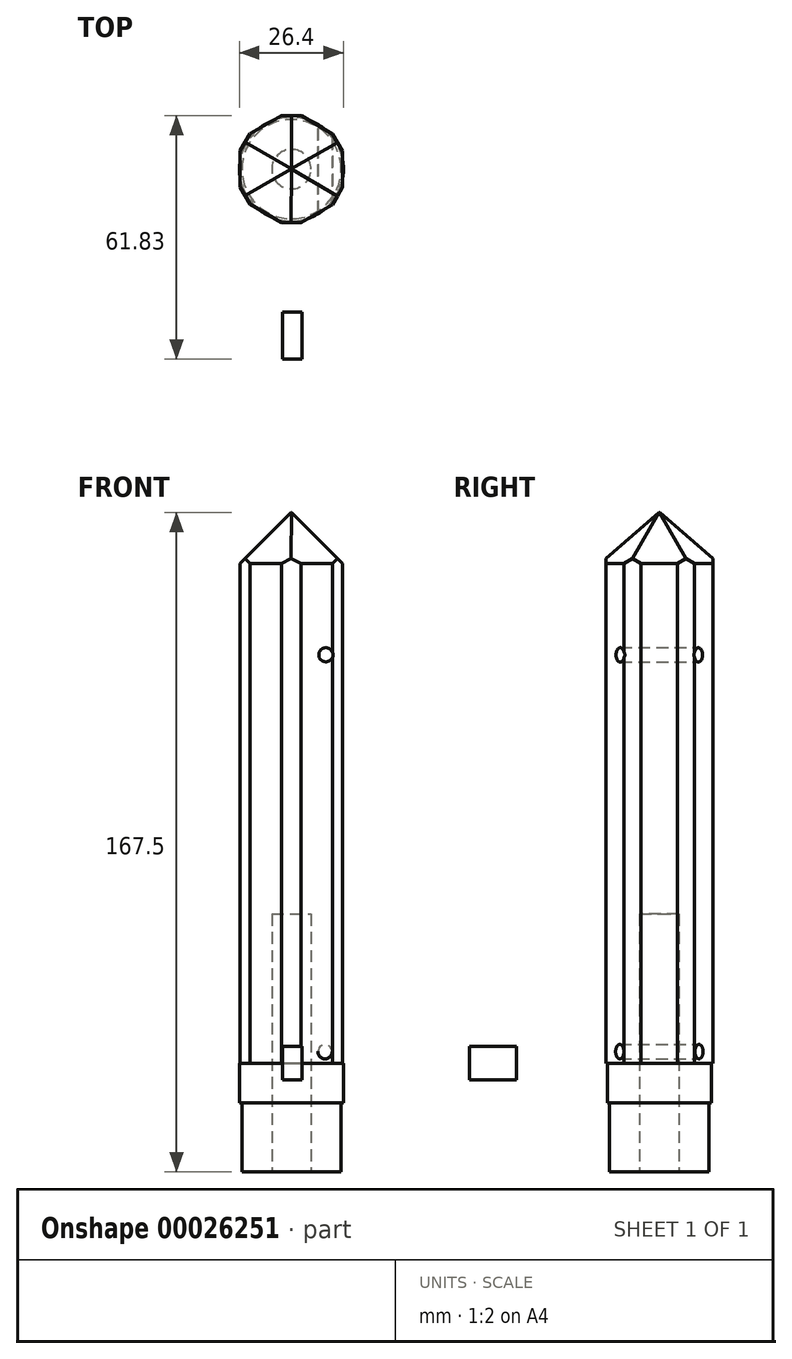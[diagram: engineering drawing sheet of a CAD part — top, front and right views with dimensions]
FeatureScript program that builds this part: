
annotation { "Feature Type Name" : "Feature", "Feature Type Description" : "" }
export const myFeature = defineFeature(function(context is Context, id is Id, definition is map)
    precondition{}
    {
        {
            var Q0;
            Q0=qCreatedBy(makeId("Front.planeOp"),FACE);
            var sketch = newSketch(context, id + "F0", { "sketchPlane" : qUnion([Q0])});
            skLineSegment(sketch, "E0.bottom", {"start": v(-84.2, -32.3) * mm, "end": v(45.8, -32.3) * mm});
            skLineSegment(sketch, "E0.top", {"start": v(-84.2, 37.7) * mm, "end": v(45.8, 37.7) * mm});
            skLineSegment(sketch, "E0.left", {"start": v(-84.2, -32.3) * mm, "end": v(-84.2, 37.7) * mm});
            skLineSegment(sketch, "E0.right", {"start": v(45.8, -32.3) * mm, "end": v(45.8, 37.7) * mm});
            skSolve(sketch);
        }
        {
            var Q0;
            Q0=makeQuery(id+"F0.imprint","IMPRINT",FACE,{"disambiguationData":[TD([[makeQuery(id+"F0.imprint","IMPRINT",EDGE,{"derivedFrom":sQuery(id+"F0.wireOp",EDGE,"E0.bottom")}),1.0]])]});
            extrude(context, id + "F1", {"entities" : qUnion([Q0]), "depth" : 40 * mm});
        }
        {
            var Q0;
            Q0=makeQuery(id+"F1.opExtrude","SWEPT_FACE",FACE,{"disambiguationData":[OSD([sQuery(id+"F0.wireOp",EDGE,"E0.left")])]});
            var sketch = newSketch(context, id + "F2", { "sketchPlane" : qUnion([Q0])});
            skCircle(sketch, "E1", {"center": v(20, 2.7) * mm, "radius": 5 * mm});
            skCircle(sketch, "E2", {"center": v(20, 2.7) * mm, "radius": 15 * mm});
            skCircle(sketch, "E3.cCircle", {"center": v(20, 2.7) * mm, "radius": 15 * mm, "construction": true});
            skLineSegment(sketch, "E3.0", {"start": v(27.46, 15.71) * mm, "end": v(35, 2.74) * mm});
            skLineSegment(sketch, "E3.1", {"start": v(35, 2.74) * mm, "end": v(27.54, -10.27) * mm});
            skLineSegment(sketch, "E3.2", {"start": v(27.54, -10.27) * mm, "end": v(12.54, -10.3) * mm});
            skLineSegment(sketch, "E3.3", {"start": v(12.54, -10.3) * mm, "end": v(5, 2.66) * mm});
            skLineSegment(sketch, "E3.4", {"start": v(5, 2.66) * mm, "end": v(12.46, 15.67) * mm});
            skLineSegment(sketch, "E3.5", {"start": v(12.46, 15.67) * mm, "end": v(27.46, 15.71) * mm});
            skSolve(sketch);
        }
        {
            var Q0;
            Q0=makeQuery(id+"F1.opExtrude","CAP_FACE",FACE,{"disambiguationData":[OSD([sQuery(id+"F0.wireOp",EDGE,"E0.bottom"),sQuery(id+"F0.wireOp",EDGE,"E0.top"),sQuery(id+"F0.wireOp",EDGE,"E0.left"),sQuery(id+"F0.wireOp",EDGE,"E0.right")])],"isStart":false});
            var sketch = newSketch(context, id + "F3", { "sketchPlane" : qUnion([Q0])});
            skCircle(sketch, "E4", {"center": v(-35.56, -24.64) * mm, "radius": 2 * mm});
            skCircle(sketch, "E5", {"center": v(174.33, -24.64) * mm, "radius": 2 * mm});
            skSolve(sketch);
        }
        {
            var Q0;
            Q0=makeQuery(id+"F3.imprint","IMPRINT",FACE,{"disambiguationData":[TD([[makeQuery(id+"F3.imprint","IMPRINT",EDGE,{"derivedFrom":sQuery(id+"F3.wireOp",EDGE,"E4")}),1.0]])]});
            var Q1;
            Q1=makeQuery(id+"F3.imprint","IMPRINT",FACE,{"disambiguationData":[TD([[makeQuery(id+"F3.imprint","IMPRINT",EDGE,{"derivedFrom":sQuery(id+"F3.wireOp",EDGE,"E5")}),1.0]])]});
            extrude(context, id + "F4", {"entities" : qUnion([Q0, Q1]), "operationType" : NewBodyOperationType.REMOVE, "endBound" : BoundingType.THROUGH_ALL, "oppositeDirection" : true, "depth" : 25 * mm});
        }
        {
            var Q0;
            {var subQ0=sQuery(id+"F0.wireOp",EDGE,"E0.left");Q0=makeQuery(id+"F2.imprint","IMPRINT",FACE,{"disambiguationData":[TD([[makeQuery(id+"F2.imprint","IMPRINT",EDGE,{"derivedFrom":makeQuery(id+"F1.opExtrude","CAP_EDGE",EDGE,{"disambiguationData":[OSD([subQ0])],"isStart":true})}),-1.0]])]});}
            extrude(context, id + "F5", {"entities" : qUnion([Q0]), "operationType" : NewBodyOperationType.REMOVE, "endBound" : BoundingType.THROUGH_ALL, "oppositeDirection" : true, "depth" : 25 * mm});
        }
        {
            var Q0;
            {var subQ0=sQuery(id+"F2.wireOp",EDGE,"E3.4");Q0=makeQuery(id+"F2.imprint","IMPRINT",FACE,{"disambiguationData":[TD([[makeQuery(id+"F2.imprint","IMPRINT",EDGE,{"derivedFrom":subQ0}),1.0]])]});}
            var Q1;
            {var subQ0=sQuery(id+"F2.wireOp",EDGE,"E3.5");Q1=makeQuery(id+"F2.imprint","IMPRINT",FACE,{"disambiguationData":[TD([[makeQuery(id+"F2.imprint","IMPRINT",EDGE,{"derivedFrom":subQ0}),1.0]])]});}
            var Q2;
            {var subQ0=sQuery(id+"F2.wireOp",EDGE,"E3.0");Q2=makeQuery(id+"F2.imprint","IMPRINT",FACE,{"disambiguationData":[TD([[makeQuery(id+"F2.imprint","IMPRINT",EDGE,{"derivedFrom":subQ0}),1.0]])]});}
            var Q3;
            {var subQ0=sQuery(id+"F2.wireOp",EDGE,"E3.1");Q3=makeQuery(id+"F2.imprint","IMPRINT",FACE,{"disambiguationData":[TD([[makeQuery(id+"F2.imprint","IMPRINT",EDGE,{"derivedFrom":subQ0}),1.0]])]});}
            var Q4;
            {var subQ0=sQuery(id+"F2.wireOp",EDGE,"E3.2");Q4=makeQuery(id+"F2.imprint","IMPRINT",FACE,{"disambiguationData":[TD([[makeQuery(id+"F2.imprint","IMPRINT",EDGE,{"derivedFrom":subQ0}),1.0]])]});}
            var Q5;
            {var subQ0=sQuery(id+"F2.wireOp",EDGE,"E3.3");Q5=makeQuery(id+"F2.imprint","IMPRINT",FACE,{"disambiguationData":[TD([[makeQuery(id+"F2.imprint","IMPRINT",EDGE,{"derivedFrom":subQ0}),1.0]])]});}
            extrude(context, id + "F6", {"entities" : qUnion([Q0, Q1, Q2, Q3, Q4, Q5]), "operationType" : NewBodyOperationType.REMOVE, "endBound" : BoundingType.THROUGH_ALL, "oppositeDirection" : true, "depth" : 25 * mm});
        }
        {
            var Q0;
            Q0=makeQuery(id+"F1.opExtrude","SWEPT_FACE",FACE,{"disambiguationData":[OSD([sQuery(id+"F0.wireOp",EDGE,"E0.right")])]});
            extrude(context, id + "F7", {"entities" : qUnion([Q0]), "operationType" : NewBodyOperationType.ADD, "depth" : 30 * mm});
        }
        {
            var Q0;
            Q0=makeQuery(id+"F7.opExtrude","CAP_EDGE",EDGE,{"disambiguationData":[OSD([sQuery(id+"F0.wireOp",EDGE,"E0.right"),sQuery(id+"F2.wireOp",EDGE,"E3.5")])],"isStart":false});
            var Q1;
            Q1=makeQuery(id+"F7.opExtrude","CAP_EDGE",EDGE,{"disambiguationData":[OSD([sQuery(id+"F0.wireOp",EDGE,"E0.right"),sQuery(id+"F2.wireOp",EDGE,"E3.0")])],"isStart":false});
            var Q2;
            Q2=makeQuery(id+"F7.opExtrude","CAP_EDGE",EDGE,{"disambiguationData":[OSD([sQuery(id+"F0.wireOp",EDGE,"E0.right"),sQuery(id+"F2.wireOp",EDGE,"E3.4")])],"isStart":false});
            var Q3;
            Q3=makeQuery(id+"F7.opExtrude","CAP_EDGE",EDGE,{"disambiguationData":[OSD([sQuery(id+"F0.wireOp",EDGE,"E0.right"),sQuery(id+"F2.wireOp",EDGE,"E3.3")])],"isStart":false});
            var Q4;
            Q4=makeQuery(id+"F7.opExtrude","CAP_EDGE",EDGE,{"disambiguationData":[OSD([sQuery(id+"F0.wireOp",EDGE,"E0.right"),sQuery(id+"F2.wireOp",EDGE,"E3.1")])],"isStart":false});
            var Q5;
            Q5=makeQuery(id+"F7.opExtrude","CAP_EDGE",EDGE,{"disambiguationData":[OSD([sQuery(id+"F0.wireOp",EDGE,"E0.right"),sQuery(id+"F2.wireOp",EDGE,"E3.2")])],"isStart":false});
            chamfer(context, id + "F8", {"entities" : qUnion([Q0, Q1, Q2, Q3, Q4, Q5]), "width" : 12.9 * mm, "tangentPropagation" : true});
        }
        {
            var Q0;
            {var subQ0=sQuery(id+"F2.wireOp",EDGE,"E2");var subQ1=sQuery(id+"F2.wireOp",EDGE,"E3.0");var subQ2=sQuery(id+"F2.wireOp",EDGE,"E3.5");Q0=makeQuery(id+"F7.boolean.opBoolean","MERGE",EDGE,{"derivedFrom":[makeQuery(id+"F6.boolean.opBoolean","TWEAK_EDGE",EDGE,{"derivedFrom":[makeQuery(id+"F6.opExtrude","SWEPT_EDGE",EDGE,{"disambiguationData":[OSD([subQ0,subQ1,subQ2]),ownerDisambiguation([makeQuery(id+"F6.opExtrude","SWEPT_BODY",BODY,{"disambiguationData":[OSD([subQ0,subQ1])]})])]}),makeQuery(id+"F6.opExtrude","SWEPT_EDGE",EDGE,{"disambiguationData":[OSD([subQ0,subQ1,subQ2]),ownerDisambiguation([makeQuery(id+"F6.opExtrude","SWEPT_BODY",BODY,{"disambiguationData":[OSD([subQ0,subQ2])]})])]})]}),makeQuery(id+"F7.opExtrude","SWEPT_EDGE",EDGE,{"disambiguationData":[OSD([sQuery(id+"F0.wireOp",EDGE,"E0.right"),subQ1,subQ2])]})]});}
            var Q1;
            {var subQ0=sQuery(id+"F2.wireOp",EDGE,"E2");var subQ1=sQuery(id+"F2.wireOp",EDGE,"E3.4");var subQ2=sQuery(id+"F2.wireOp",EDGE,"E3.5");Q1=makeQuery(id+"F7.boolean.opBoolean","MERGE",EDGE,{"derivedFrom":[makeQuery(id+"F6.boolean.opBoolean","TWEAK_EDGE",EDGE,{"derivedFrom":[makeQuery(id+"F6.opExtrude","SWEPT_EDGE",EDGE,{"disambiguationData":[OSD([subQ0,subQ1,subQ2]),ownerDisambiguation([makeQuery(id+"F6.opExtrude","SWEPT_BODY",BODY,{"disambiguationData":[OSD([subQ0,subQ2])]})])]}),makeQuery(id+"F6.opExtrude","SWEPT_EDGE",EDGE,{"disambiguationData":[OSD([subQ0,subQ1,subQ2]),ownerDisambiguation([makeQuery(id+"F6.opExtrude","SWEPT_BODY",BODY,{"disambiguationData":[OSD([subQ0,subQ1])]})])]})]}),makeQuery(id+"F7.opExtrude","SWEPT_EDGE",EDGE,{"disambiguationData":[OSD([sQuery(id+"F0.wireOp",EDGE,"E0.right"),subQ1,subQ2])]})]});}
            var Q2;
            {var subQ0=sQuery(id+"F2.wireOp",EDGE,"E2");var subQ1=sQuery(id+"F2.wireOp",EDGE,"E3.0");var subQ2=sQuery(id+"F2.wireOp",EDGE,"E3.1");Q2=makeQuery(id+"F7.boolean.opBoolean","MERGE",EDGE,{"derivedFrom":[makeQuery(id+"F6.boolean.opBoolean","TWEAK_EDGE",EDGE,{"derivedFrom":[makeQuery(id+"F6.opExtrude","SWEPT_EDGE",EDGE,{"disambiguationData":[OSD([subQ0,subQ1,subQ2]),ownerDisambiguation([makeQuery(id+"F6.opExtrude","SWEPT_BODY",BODY,{"disambiguationData":[OSD([subQ0,subQ1])]})])]}),makeQuery(id+"F6.opExtrude","SWEPT_EDGE",EDGE,{"disambiguationData":[OSD([subQ0,subQ1,subQ2]),ownerDisambiguation([makeQuery(id+"F6.opExtrude","SWEPT_BODY",BODY,{"disambiguationData":[OSD([subQ0,subQ2])]})])]})]}),makeQuery(id+"F7.opExtrude","SWEPT_EDGE",EDGE,{"disambiguationData":[OSD([sQuery(id+"F0.wireOp",EDGE,"E0.right"),subQ1,subQ2])]})]});}
            var Q3;
            {var subQ0=sQuery(id+"F2.wireOp",EDGE,"E2");var subQ1=sQuery(id+"F2.wireOp",EDGE,"E3.1");var subQ2=sQuery(id+"F2.wireOp",EDGE,"E3.2");Q3=makeQuery(id+"F7.boolean.opBoolean","MERGE",EDGE,{"derivedFrom":[makeQuery(id+"F6.boolean.opBoolean","TWEAK_EDGE",EDGE,{"derivedFrom":[makeQuery(id+"F6.opExtrude","SWEPT_EDGE",EDGE,{"disambiguationData":[OSD([subQ0,subQ1,subQ2]),ownerDisambiguation([makeQuery(id+"F6.opExtrude","SWEPT_BODY",BODY,{"disambiguationData":[OSD([subQ0,subQ2])]})])]}),makeQuery(id+"F6.opExtrude","SWEPT_EDGE",EDGE,{"disambiguationData":[OSD([subQ0,subQ1,subQ2]),ownerDisambiguation([makeQuery(id+"F6.opExtrude","SWEPT_BODY",BODY,{"disambiguationData":[OSD([subQ0,subQ1])]})])]})]}),makeQuery(id+"F7.opExtrude","SWEPT_EDGE",EDGE,{"disambiguationData":[OSD([sQuery(id+"F0.wireOp",EDGE,"E0.right"),subQ1,subQ2])]})]});}
            var Q4;
            {var subQ0=sQuery(id+"F2.wireOp",EDGE,"E2");var subQ1=sQuery(id+"F2.wireOp",EDGE,"E3.3");var subQ2=sQuery(id+"F2.wireOp",EDGE,"E3.4");Q4=makeQuery(id+"F7.boolean.opBoolean","MERGE",EDGE,{"derivedFrom":[makeQuery(id+"F6.boolean.opBoolean","TWEAK_EDGE",EDGE,{"derivedFrom":[makeQuery(id+"F6.opExtrude","SWEPT_EDGE",EDGE,{"disambiguationData":[OSD([subQ0,subQ1,subQ2]),ownerDisambiguation([makeQuery(id+"F6.opExtrude","SWEPT_BODY",BODY,{"disambiguationData":[OSD([subQ0,subQ2])]})])]}),makeQuery(id+"F6.opExtrude","SWEPT_EDGE",EDGE,{"disambiguationData":[OSD([subQ0,subQ1,subQ2]),ownerDisambiguation([makeQuery(id+"F6.opExtrude","SWEPT_BODY",BODY,{"disambiguationData":[OSD([subQ0,subQ1])]})])]})]}),makeQuery(id+"F7.opExtrude","SWEPT_EDGE",EDGE,{"disambiguationData":[OSD([sQuery(id+"F0.wireOp",EDGE,"E0.right"),subQ1,subQ2])]})]});}
            var Q5;
            {var subQ0=sQuery(id+"F2.wireOp",EDGE,"E2");var subQ1=sQuery(id+"F2.wireOp",EDGE,"E3.2");var subQ2=sQuery(id+"F2.wireOp",EDGE,"E3.3");Q5=makeQuery(id+"F7.boolean.opBoolean","MERGE",EDGE,{"derivedFrom":[makeQuery(id+"F6.boolean.opBoolean","TWEAK_EDGE",EDGE,{"derivedFrom":[makeQuery(id+"F6.opExtrude","SWEPT_EDGE",EDGE,{"disambiguationData":[OSD([subQ0,subQ1,subQ2]),ownerDisambiguation([makeQuery(id+"F6.opExtrude","SWEPT_BODY",BODY,{"disambiguationData":[OSD([subQ0,subQ2])]})])]}),makeQuery(id+"F6.opExtrude","SWEPT_EDGE",EDGE,{"disambiguationData":[OSD([subQ0,subQ1,subQ2]),ownerDisambiguation([makeQuery(id+"F6.opExtrude","SWEPT_BODY",BODY,{"disambiguationData":[OSD([subQ0,subQ1])]})])]})]}),makeQuery(id+"F7.opExtrude","SWEPT_EDGE",EDGE,{"disambiguationData":[OSD([sQuery(id+"F0.wireOp",EDGE,"E0.right"),subQ1,subQ2])]})]});}
            chamfer(context, id + "F9", {"entities" : qUnion([Q0, Q1, Q2, Q3, Q4, Q5]), "width" : 5 * mm, "tangentPropagation" : true});
        }
        {
            var Q0;
            Q0=qCreatedBy(makeId("Front.planeOp"),FACE);
            var sketch = newSketch(context, id + "F10", { "sketchPlane" : qUnion([Q0])});
            skCircle(sketch, "E6", {"center": v(-61.16, -5.86) * mm, "radius": 1.83 * mm});
            skCircle(sketch, "E7", {"center": v(39.65, -6.06) * mm, "radius": 1.83 * mm});
            skSolve(sketch);
        }
        {
            var Q0;
            Q0=makeQuery(id+"F10.imprint","IMPRINT",FACE,{"disambiguationData":[TD([[makeQuery(id+"F10.imprint","IMPRINT",EDGE,{"derivedFrom":sQuery(id+"F10.wireOp",EDGE,"E7")}),1.0]])]});
            var Q1;
            Q1=makeQuery(id+"F10.imprint","IMPRINT",FACE,{"disambiguationData":[TD([[makeQuery(id+"F10.imprint","IMPRINT",EDGE,{"derivedFrom":sQuery(id+"F10.wireOp",EDGE,"E6")}),1.0]])]});
            extrude(context, id + "F11", {"entities" : qUnion([Q0, Q1]), "operationType" : NewBodyOperationType.REMOVE, "endBound" : BoundingType.THROUGH_ALL, "depth" : 25 * mm});
        }
        {
            var Q0;
            Q0=makeQuery(id+"F1.opExtrude","SWEPT_FACE",FACE,{"disambiguationData":[OSD([sQuery(id+"F0.wireOp",EDGE,"E0.left")])]});
            extrude(context, id + "F12", {"entities" : qUnion([Q0]), "operationType" : NewBodyOperationType.REMOVE, "oppositeDirection" : true, "depth" : 20 * mm});
        }
        {
            var Q0;
            Q0=makeQuery(id+"F12.boolean.opBoolean","COPY",FACE,{"derivedFrom":makeQuery(id+"F12.opExtrude","CAP_FACE",FACE,{"disambiguationData":[OSD([sQuery(id+"F0.wireOp",EDGE,"E0.left")])],"isStart":false})});
            var sketch = newSketch(context, id + "F13", { "sketchPlane" : qUnion([Q0])});
            skPoint(sketch, "E8", {"position": v(20.02, 2.68) * mm});
            skCircle(sketch, "E9", {"center": v(20.02, 2.68) * mm, "radius": 13.2 * mm});
            skSolve(sketch);
        }
        {
            var Q0;
            Q0=qSketchRegion(id+"F13",true);
            extrude(context, id + "F14", {"entities" : qUnion([Q0]), "operationType" : NewBodyOperationType.ADD, "depth" : 10 * mm});
        }
        {
            var Q0;
            Q0=makeQuery(id+"F14.opExtrude","CAP_FACE",FACE,{"disambiguationData":[OSD([sQuery(id+"F13.wireOp",EDGE,"E9")])],"isStart":false});
            var sketch = newSketch(context, id + "F15", { "sketchPlane" : qUnion([Q0])});
            skCircle(sketch, "E10", {"center": v(20.02, 2.68) * mm, "radius": 12.6 * mm});
            skSolve(sketch);
        }
        {
            var Q0;
            Q0=qSketchRegion(id+"F15",true);
            extrude(context, id + "F16", {"entities" : qUnion([Q0]), "operationType" : NewBodyOperationType.ADD, "depth" : 17.5 * mm});
        }
        {
            var Q0;
            Q0=makeQuery(id+"F16.opExtrude","CAP_FACE",FACE,{"disambiguationData":[OSD([sQuery(id+"F15.wireOp",EDGE,"E10")])],"isStart":false});
            var sketch = newSketch(context, id + "F17", { "sketchPlane" : qUnion([Q0])});
            skCircle(sketch, "E11", {"center": v(20.02, 2.68) * mm, "radius": 5 * mm});
            skSolve(sketch);
        }
        {
            var Q0;
            Q0=makeQuery(id+"F17.imprint","IMPRINT",FACE,{"disambiguationData":[TD([[makeQuery(id+"F17.imprint","IMPRINT",EDGE,{"derivedFrom":sQuery(id+"F17.wireOp",EDGE,"E11")}),1.0]])]});
            extrude(context, id + "F18", {"entities" : qUnion([Q0]), "operationType" : NewBodyOperationType.REMOVE, "oppositeDirection" : true, "depth" : 65.5 * mm});
        }
        {
            var Q0;
            Q0=qCreatedBy(makeId("Top.planeOp"),FACE);
            var sketch = newSketch(context, id + "F19", { "sketchPlane" : qUnion([Q0])});
            skLineSegment(sketch, "E12.bottom", {"start": v(-68.34, -68.27) * mm, "end": v(-59.86, -68.27) * mm});
            skLineSegment(sketch, "E12.top", {"start": v(-68.34, -56.3) * mm, "end": v(-59.86, -56.3) * mm});
            skLineSegment(sketch, "E12.left", {"start": v(-68.34, -68.27) * mm, "end": v(-68.34, -56.3) * mm});
            skLineSegment(sketch, "E12.right", {"start": v(-59.86, -68.27) * mm, "end": v(-59.86, -56.3) * mm});
            skSolve(sketch);
        }
        {
            var Q0;
            Q0=makeQuery(id+"F19.imprint","IMPRINT",FACE,{"disambiguationData":[TD([[makeQuery(id+"F19.imprint","IMPRINT",EDGE,{"derivedFrom":sQuery(id+"F19.wireOp",EDGE,"E12.bottom")}),1.0]])]});
            extrude(context, id + "F20", {"entities" : qUnion([Q0]), "depth" : 5 * mm});
        }
        {
            var Q0;
            Q0=makeQuery(id+"F1.opExtrude","SWEPT_BODY",BODY,{"disambiguationData":[OSD([sQuery(id+"F0.wireOp",EDGE,"E0.bottom"),sQuery(id+"F0.wireOp",EDGE,"E0.top"),sQuery(id+"F0.wireOp",EDGE,"E0.left"),sQuery(id+"F0.wireOp",EDGE,"E0.right")])]});
            var Q1;
            Q1=makeQuery(id+"F20.opExtrude","SWEPT_BODY",BODY,{"disambiguationData":[OSD([sQuery(id+"F19.wireOp",EDGE,"E12.bottom"),sQuery(id+"F19.wireOp",EDGE,"E12.top"),sQuery(id+"F19.wireOp",EDGE,"E12.left"),sQuery(id+"F19.wireOp",EDGE,"E12.right")])]});
            var Q2;
            Q2=makeQuery(id+"F20.opExtrude","CAP_EDGE",EDGE,{"disambiguationData":[OSD([sQuery(id+"F19.wireOp",EDGE,"E12.left")])],"isStart":false});
            transform(context, id + "F21", {"entities" : qUnion([Q0, Q1]), "transformType" : TransformType.ROTATION, "transformAxis" : qUnion([Q2]), "angle" : 90 * degree, "oppositeDirection" : true, "makeCopy" : false});
        }
    });
